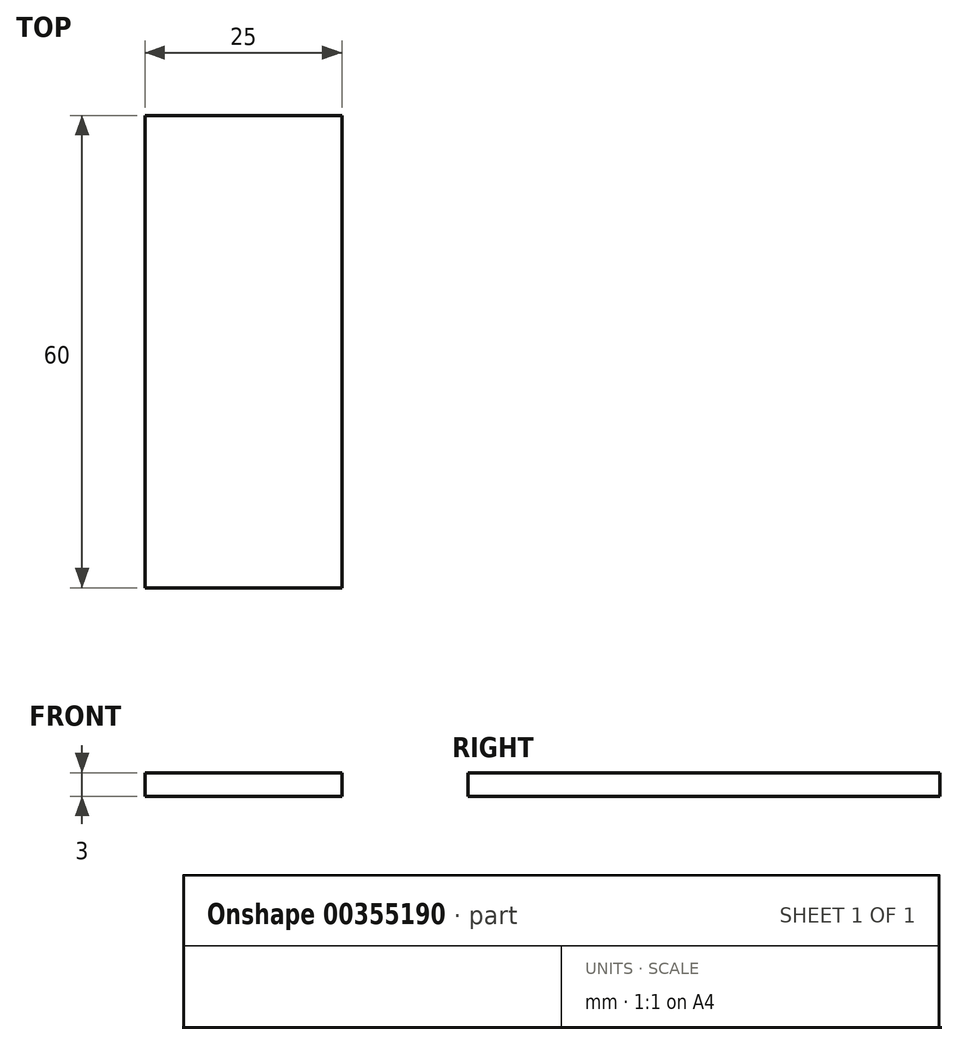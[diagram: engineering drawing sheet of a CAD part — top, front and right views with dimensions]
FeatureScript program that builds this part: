
annotation { "Feature Type Name" : "Feature", "Feature Type Description" : "" }
export const myFeature = defineFeature(function(context is Context, id is Id, definition is map)
    precondition{}
    {
        {
            var Q0;
            Q0=qCreatedBy(makeId("Top.planeOp"),FACE);
            var sketch = newSketch(context, id + "F0", { "sketchPlane" : qUnion([Q0])});
            skLineSegment(sketch, "E0", {"start": v(-55.67, 53.97) * mm, "end": v(-55.67, -6.03) * mm});
            skLineSegment(sketch, "E1", {"start": v(-55.67, -6.03) * mm, "end": v(-30.67, -6.03) * mm});
            skLineSegment(sketch, "E2", {"start": v(-30.67, -6.03) * mm, "end": v(-30.67, 53.97) * mm});
            skLineSegment(sketch, "E3", {"start": v(-55.67, 53.97) * mm, "end": v(-30.67, 53.97) * mm});
            skSolve(sketch);
        }
        {
            var Q0;
            Q0=makeQuery(id+"F0.imprint","IMPRINT",FACE,{"disambiguationData":[TD([[makeQuery(id+"F0.imprint","IMPRINT",EDGE,{"derivedFrom":sQuery(id+"F0.wireOp",EDGE,"E0")}),1.0]])]});
            extrude(context, id + "F1", {"entities" : qUnion([Q0]), "depth" : 3 * mm});
        }
    });
